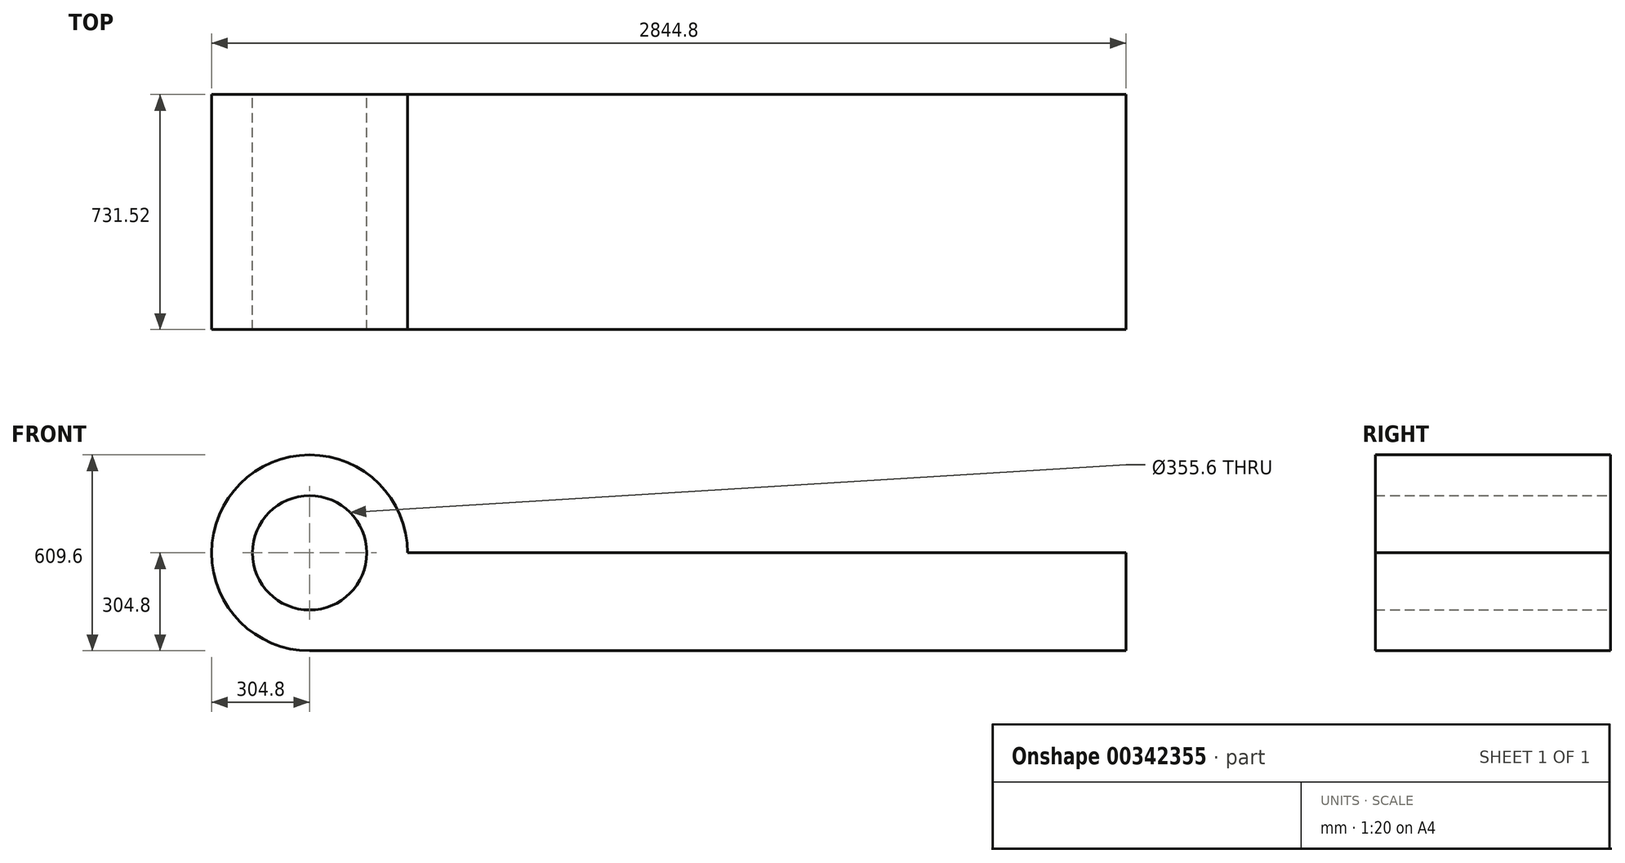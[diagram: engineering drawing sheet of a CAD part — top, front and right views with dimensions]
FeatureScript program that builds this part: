
annotation { "Feature Type Name" : "Feature", "Feature Type Description" : "" }
export const myFeature = defineFeature(function(context is Context, id is Id, definition is map)
    precondition{}
    {
        {
            var Q0;
            Q0=qCreatedBy(makeId("Front.planeOp"),FACE);
            var sketch = newSketch(context, id + "F0", { "sketchPlane" : qUnion([Q0])});
            skArc(sketch, "E0", {"start": v(304.8, 0) * mm, "mid": v(-215.53, 215.53) * mm, "end": v(0, -304.8) * mm});
            skCircle(sketch, "E1", {"center": v(0, 0) * mm, "radius": 177.8 * mm});
            skLineSegment(sketch, "E2.bottom", {"start": v(0, -304.8) * mm, "end": v(2540, -304.8) * mm});
            skLineSegment(sketch, "E2.right", {"start": v(2540, -304.8) * mm, "end": v(2540, 0) * mm});
            skLineSegment(sketch, "E3.trimOffspring", {"start": v(304.8, 0) * mm, "end": v(2540, 0) * mm});
            skSolve(sketch);
        }
        {
            var Q0;
            Q0 = qSketchRegion(id + "F0", true);
            extrude(context, id + "F1", {"entities" : qUnion([Q0]), "endBound" : BoundingType.SYMMETRIC, "depth" : 731.52 * mm});
        }
    });
